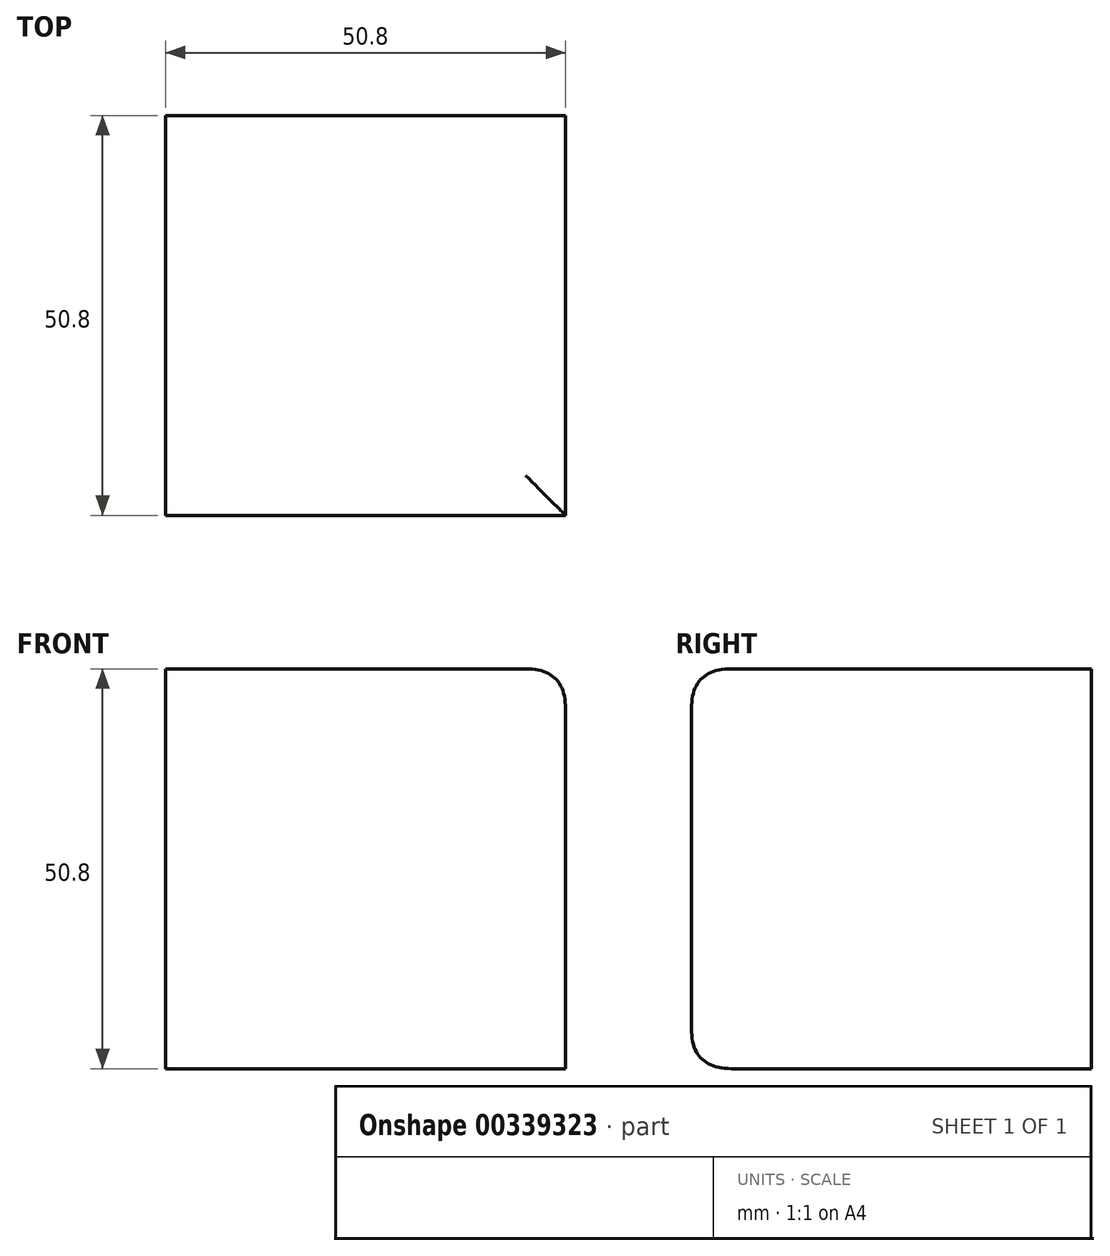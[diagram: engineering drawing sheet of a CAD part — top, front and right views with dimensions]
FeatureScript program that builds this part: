
annotation { "Feature Type Name" : "Feature", "Feature Type Description" : "" }
export const myFeature = defineFeature(function(context is Context, id is Id, definition is map)
    precondition{}
    {
        {
            var Q0;
            Q0=qCreatedBy(makeId("Front.planeOp"),FACE);
            var sketch = newSketch(context, id + "F0", { "sketchPlane" : qUnion([Q0])});
            skLineSegment(sketch, "E0.bottom", {"start": v(0, 0) * mm, "end": v(50.8, 0) * mm});
            skLineSegment(sketch, "E0.top", {"start": v(0, 50.8) * mm, "end": v(50.8, 50.8) * mm});
            skLineSegment(sketch, "E0.left", {"start": v(0, 0) * mm, "end": v(0, 50.8) * mm});
            skLineSegment(sketch, "E0.right", {"start": v(50.8, 0) * mm, "end": v(50.8, 50.8) * mm});
            skSolve(sketch);
        }
        {
            var Q0;
            Q0 = qSketchRegion(id + "F0", true);
            extrude(context, id + "F1", {"entities" : qUnion([Q0]), "depth" : 50.8 * mm});
        }
        {
            var Q0;
            Q0=makeQuery(id+"F1.opExtrude","SWEPT_EDGE",EDGE,{"disambiguationData":[OSD([sQuery(id+"F0.wireOp",EDGE,"E0.top"),sQuery(id+"F0.wireOp",EDGE,"E0.right")])]});
            var Q1;
            Q1=makeQuery(id+"F1.opExtrude","CAP_EDGE",EDGE,{"disambiguationData":[OSD([sQuery(id+"F0.wireOp",EDGE,"E0.top")])],"isStart":false});
            fillet(context, id + "F2", {"entities" : qUnion([Q0, Q1]), "radius" : 5.08 * mm, "tangentPropagation" : true, "rho" : 0.5, "crossSection" : FilletCrossSection.CONIC, "allowEdgeOverflow" : false});
        }
        {
            var Q0;
            Q0=makeQuery(id+"F1.opExtrude","CAP_EDGE",EDGE,{"disambiguationData":[OSD([sQuery(id+"F0.wireOp",EDGE,"E0.bottom")])],"isStart":false});
            fillet(context, id + "F3", {"entities" : qUnion([Q0]), "radius" : 5.08 * mm, "tangentPropagation" : true, "rho" : 0.5, "crossSection" : FilletCrossSection.CONIC, "allowEdgeOverflow" : false});
        }
    });
